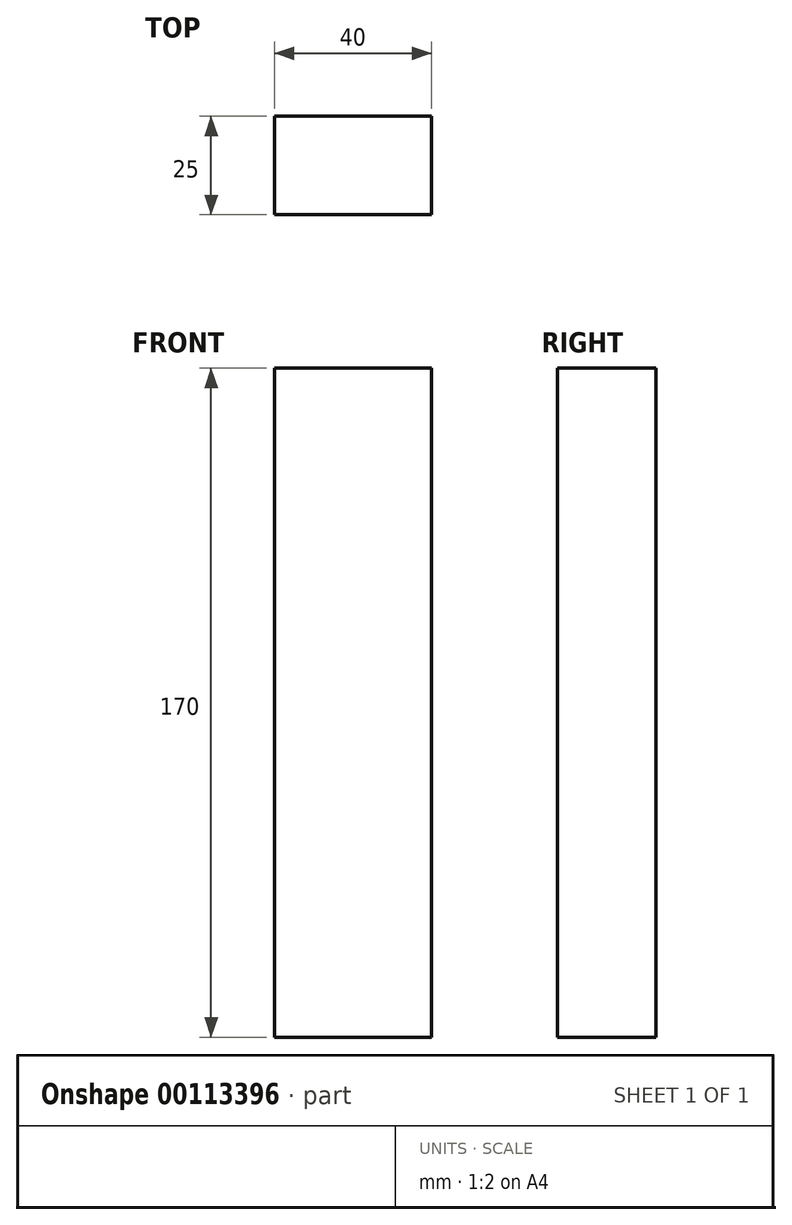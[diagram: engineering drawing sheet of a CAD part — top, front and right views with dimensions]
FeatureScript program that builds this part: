
annotation { "Feature Type Name" : "Feature", "Feature Type Description" : "" }
export const myFeature = defineFeature(function(context is Context, id is Id, definition is map)
    precondition{}
    {
        {
            var Q0;
            Q0=qCreatedBy(makeId("Front.planeOp"),FACE);
            var sketch = newSketch(context, id + "F0", { "sketchPlane" : qUnion([Q0])});
            skLineSegment(sketch, "E0", {"start": v(0, 0) * mm, "end": v(0, 170) * mm});
            skLineSegment(sketch, "E1", {"start": v(0, 170) * mm, "end": v(40, 170) * mm});
            skLineSegment(sketch, "E2", {"start": v(40, 170) * mm, "end": v(40, 0) * mm});
            skLineSegment(sketch, "E3", {"start": v(40, 0) * mm, "end": v(0, 0) * mm});
            skSolve(sketch);
        }
        {
            var Q0;
            Q0=makeQuery(id+"F0.imprint","IMPRINT",FACE,{"disambiguationData":[TD([[makeQuery(id+"F0.imprint","IMPRINT",EDGE,{"derivedFrom":sQuery(id+"F0.wireOp",EDGE,"E0")}),-1.0]])]});
            extrude(context, id + "F1", {"entities" : qUnion([Q0]), "depth" : 25 * mm});
        }
    });
